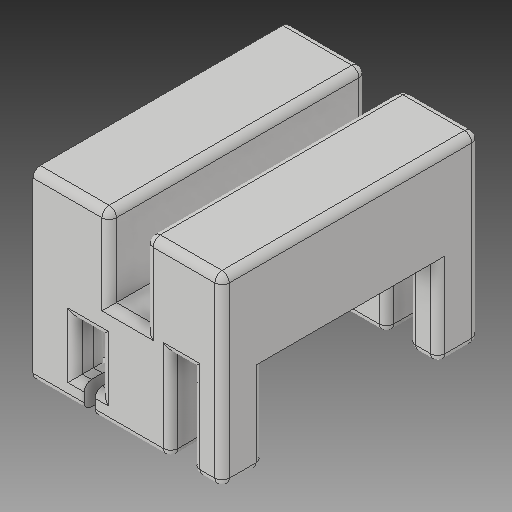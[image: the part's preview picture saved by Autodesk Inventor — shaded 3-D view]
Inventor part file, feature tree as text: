
AUTODESK INVENTOR PART (.ipt)
format: ipt  version: 2018 (Build 220112000, 112)  size: 307,712 bytes
history: native  units: in
note: dims shown in document units (in); Inventor stores cm internally (conversion verified against a paired STEP export)
features: sketch x22, other x3, plane x2
ambient origin geometry x8: Origin, YZ Plane, XZ Plane, XY Plane, X Axis, Y Axis, Z Axis, Center Point
bodies: Solid1 (feature_tree)
feature tree (27):
  other  "newShoulder.ipt"
  other  "Solid1::newShoulder.ipt"
  other  "TaggingFeature1"
  sketch  "Sketch1"  dims[d0=0.3937in]
  sketch  "Sketch2"
  sketch  "Sketch3"
  sketch  "Sketch4"
  sketch  "Sketch5"
  sketch  "Sketch6"
  sketch  "Sketch7"
  sketch  "Sketch8"
  sketch  "Sketch11"
  sketch  "Sketch12"
  sketch  "Sketch13"
  sketch  "Sketch14"
  sketch  "Sketch15"
  sketch  "Sketch17"
  sketch  "Sketch18"
  sketch  "Sketch19"
  sketch  "Sketch20"
  sketch  "Sketch21"
  sketch  "Sketch22"
  sketch  "Sketch23"
  sketch  "Sketch24"
  sketch  "Sketch27"
  plane  "Work Plane1"
  plane  "Work Plane2"
